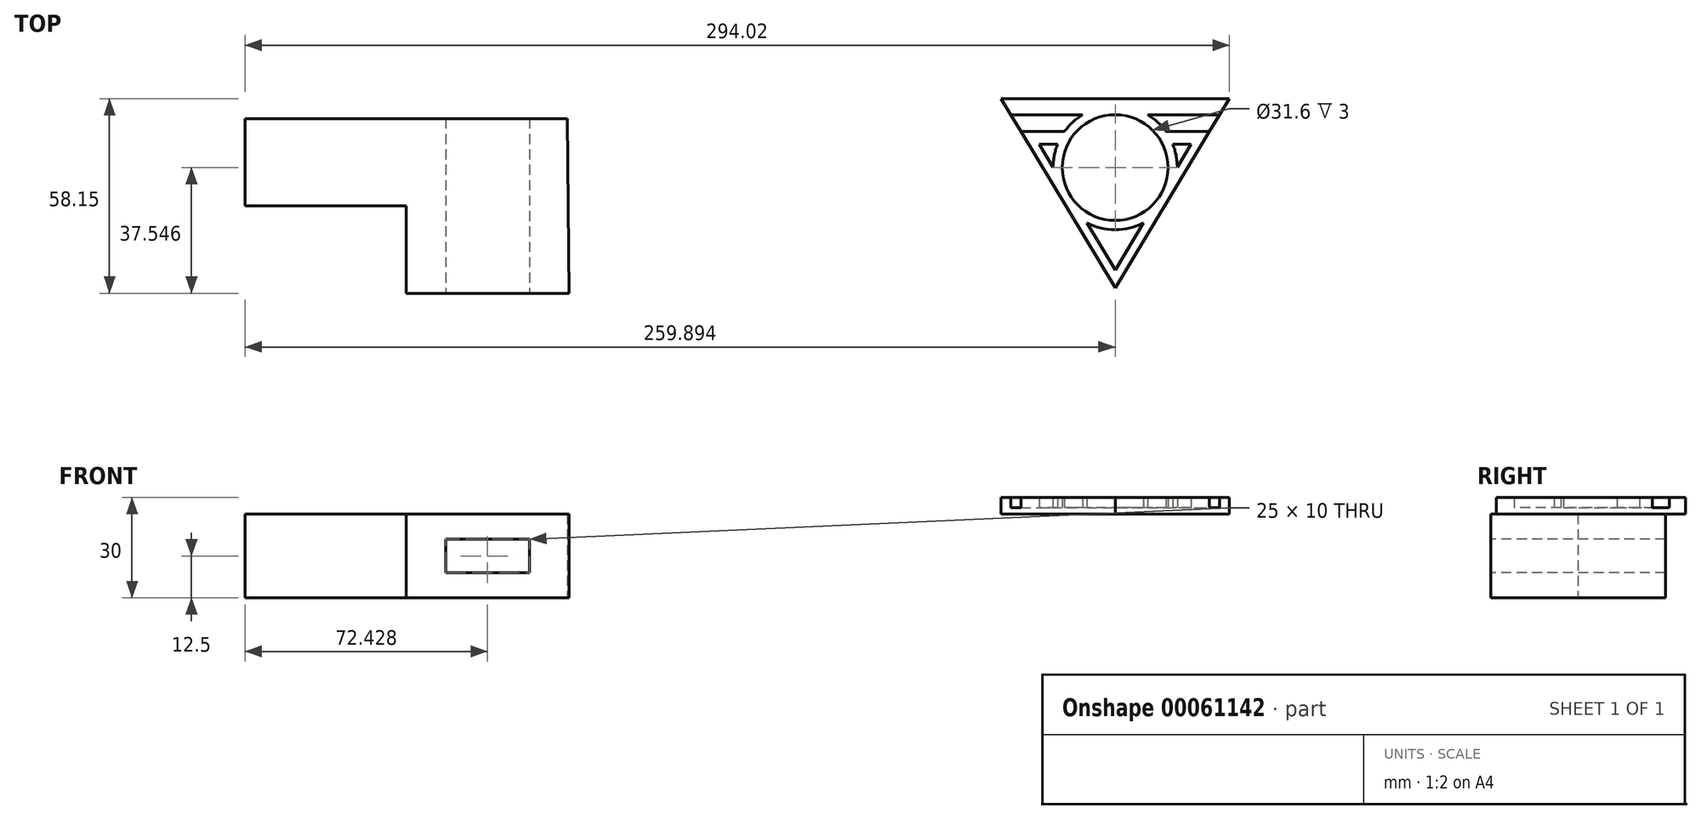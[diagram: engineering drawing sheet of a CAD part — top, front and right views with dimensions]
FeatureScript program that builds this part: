
annotation { "Feature Type Name" : "Feature", "Feature Type Description" : "" }
export const myFeature = defineFeature(function(context is Context, id is Id, definition is map)
    precondition{}
    {
        {
            var Q0;
            Q0=qCreatedBy(makeId("Top.planeOp"),FACE);
            var sketch = newSketch(context, id + "F0", { "sketchPlane" : qUnion([Q0])});
            skLineSegment(sketch, "E0", {"start": v(-34, 20.87) * mm, "end": v(62.24, 20.87) * mm});
            skLineSegment(sketch, "E1", {"start": v(62.24, 20.87) * mm, "end": v(62.74, -31.3) * mm});
            skLineSegment(sketch, "E2", {"start": v(62.74, -31.3) * mm, "end": v(14.12, -31.3) * mm});
            skPoint(sketch, "E2.endSnap0", {"position": v(14.12, 20.87) * mm});
            skLineSegment(sketch, "E3", {"start": v(14.12, -31.3) * mm, "end": v(14.12, -5.21) * mm});
            skPoint(sketch, "E3.endSnap0", {"position": v(62.49, -5.21) * mm});
            skLineSegment(sketch, "E4", {"start": v(14.12, -5.21) * mm, "end": v(-34, -5.21) * mm});
            skLineSegment(sketch, "E5", {"start": v(-34, -5.21) * mm, "end": v(-34, 20.87) * mm});
            skSolve(sketch);
        }
        {
            var Q0;
            Q0 = qSketchRegion(id + "F0", true);
            extrude(context, id + "F1", {"entities" : qUnion([Q0]), "depth" : 25 * mm});
        }
        {
            var Q0;
            Q0=makeQuery(id+"F1.opExtrude","SWEPT_FACE",FACE,{"disambiguationData":[OSD([sQuery(id+"F0.wireOp",EDGE,"E2")])]});
            var sketch = newSketch(context, id + "F2", { "sketchPlane" : qUnion([Q0])});
            skLineSegment(sketch, "E6.rect.bottom", {"start": v(50.93, 7.5) * mm, "end": v(25.93, 7.5) * mm});
            skLineSegment(sketch, "E6.rect.top", {"start": v(50.93, 17.5) * mm, "end": v(25.93, 17.5) * mm});
            skLineSegment(sketch, "E6.rect.left", {"start": v(50.93, 7.5) * mm, "end": v(50.93, 17.5) * mm});
            skLineSegment(sketch, "E6.rect.right", {"start": v(25.93, 7.5) * mm, "end": v(25.93, 17.5) * mm});
            skPoint(sketch, "E6.rect.middle", {"position": v(38.43, 12.5) * mm});
            skPoint(sketch, "E6.rect.middle.positionSnap0", {"position": v(62.74, 12.5) * mm});
            skPoint(sketch, "E6.rect.middle.positionSnap1", {"position": v(38.43, 25) * mm});
            skPoint(sketch, "E6.rect.centerSnap0", {"position": v(62.74, 12.5) * mm});
            skPoint(sketch, "E6.rect.centerSnap1", {"position": v(38.43, 25) * mm});
            skSolve(sketch);
        }
        {
            var Q0;
            Q0 = qSketchRegion(id + "F2", true);
            extrude(context, id + "F3", {"entities" : qUnion([Q0]), "operationType" : NewBodyOperationType.REMOVE, "endBound" : BoundingType.THROUGH_ALL, "oppositeDirection" : true, "depth" : 57.6 * mm});
        }
        {
            var Q0;
            Q0=makeQuery(id+"F1.opExtrude","CAP_FACE",FACE,{"disambiguationData":[OSD([sQuery(id+"F0.wireOp",EDGE,"E0"),sQuery(id+"F0.wireOp",EDGE,"E1"),sQuery(id+"F0.wireOp",EDGE,"E2"),sQuery(id+"F0.wireOp",EDGE,"E3"),sQuery(id+"F0.wireOp",EDGE,"E4"),sQuery(id+"F0.wireOp",EDGE,"E5")])],"isStart":false});
            var sketch = newSketch(context, id + "F4", { "sketchPlane" : qUnion([Q0])});
            skLineSegment(sketch, "E7", {"start": v(225.9, -29.64) * mm, "end": v(191.77, 26.85) * mm});
            skLineSegment(sketch, "E8", {"start": v(191.77, 26.85) * mm, "end": v(225.9, 26.85) * mm});
            skLineSegment(sketch, "E9", {"start": v(225.9, 26.85) * mm, "end": v(225.9, -29.64) * mm, "construction": true});
            skLineSegment(sketch, "E10.MirrorCS", {"start": v(260.02, 26.85) * mm, "end": v(225.9, 26.85) * mm});
            skLineSegment(sketch, "E11.MirrorCS", {"start": v(225.9, -29.64) * mm, "end": v(260.02, 26.85) * mm});
            skSolve(sketch);
        }
        {
            var Q0;
            Q0 = qSketchRegion(id + "F4", true);
            extrude(context, id + "F5", {"entities" : qUnion([Q0]), "depth" : 2 * mm});
        }
        {
            var Q0;
            Q0=makeQuery(id+"F5.opExtrude","CAP_FACE",FACE,{"disambiguationData":[OSD([sQuery(id+"F4.wireOp",EDGE,"E7"),sQuery(id+"F4.wireOp",EDGE,"E8"),sQuery(id+"F4.wireOp",EDGE,"E10.MirrorCS"),sQuery(id+"F4.wireOp",EDGE,"E11.MirrorCS")])],"isStart":false});
            var sketch = newSketch(context, id + "F6", { "sketchPlane" : qUnion([Q0])});
            skLineSegment(sketch, "E12", {"start": v(191.77, 26.85) * mm, "end": v(194.67, 22.05) * mm});
            skLineSegment(sketch, "E13", {"start": v(194.67, 22.05) * mm, "end": v(216.16, 22.05) * mm});
            skLineSegment(sketch, "E14", {"start": v(257.12, 22.05) * mm, "end": v(260.02, 26.85) * mm});
            skLineSegment(sketch, "E15", {"start": v(260.02, 26.85) * mm, "end": v(191.77, 26.85) * mm});
            skLineSegment(sketch, "E16", {"start": v(197.73, 16.97) * mm, "end": v(210.75, 16.97) * mm});
            skLineSegment(sketch, "E17", {"start": v(254.06, 16.97) * mm, "end": v(251.77, 13.2) * mm});
            skLineSegment(sketch, "E18", {"start": v(251.77, 13.2) * mm, "end": v(243.1, 13.2) * mm});
            skLineSegment(sketch, "E19", {"start": v(200.02, 13.2) * mm, "end": v(197.73, 16.97) * mm});
            skLineSegment(sketch, "E20", {"start": v(225.9, -29.64) * mm, "end": v(225.9, 26.85) * mm, "construction": true});
            skLineSegment(sketch, "E21", {"start": v(203.23, 13.2) * mm, "end": v(207.34, 6.4) * mm});
            skLineSegment(sketch, "E22.MirrorCS", {"start": v(248.55, 13.2) * mm, "end": v(244.45, 6.4) * mm});
            skArc(sketch, "E23", {"start": v(216.16, 22.05) * mm, "mid": v(213.2, 19.78) * mm, "end": v(210.75, 16.97) * mm});
            skCircle(sketch, "E24", {"center": v(225.9, 6.25) * mm, "radius": 15.8 * mm});
            skLineSegment(sketch, "E25.trimOffspring", {"start": v(235.63, 22.05) * mm, "end": v(257.12, 22.05) * mm});
            skLineSegment(sketch, "E26.trimOffspring", {"start": v(208.69, 13.2) * mm, "end": v(203.23, 13.2) * mm});
            skArc(sketch, "E27.trimOffspring", {"start": v(208.69, 13.2) * mm, "mid": v(207.7, 9.86) * mm, "end": v(207.34, 6.4) * mm});
            skArc(sketch, "E28.trimOffspring", {"start": v(217.4, -10.25) * mm, "mid": v(238.4, -7.47) * mm, "end": v(243.1, 13.2) * mm});
            skLineSegment(sketch, "E29.trimOffspring", {"start": v(217.4, -10.25) * mm, "end": v(225.9, -24.31) * mm});
            skLineSegment(sketch, "E30.trimOffspring", {"start": v(234.39, -10.25) * mm, "end": v(225.9, -24.31) * mm});
            skLineSegment(sketch, "E31.trimOffspring", {"start": v(241.04, 16.97) * mm, "end": v(254.06, 16.97) * mm});
            skArc(sketch, "E32.trimOffspring", {"start": v(241.04, 16.97) * mm, "mid": v(238.59, 19.78) * mm, "end": v(235.63, 22.05) * mm});
            skSolve(sketch);
        }
        {
            var Q0;
            Q0=makeQuery(id+"F6.imprint","IMPRINT",FACE,{"disambiguationData":[TD([[makeQuery(id+"F6.imprint","IMPRINT",EDGE,{"derivedFrom":sQuery(id+"F6.wireOp",EDGE,"E12")}),-1.0]])]});
            var Q1;
            {var subQ3=sQuery(id+"F6.wireOp",EDGE,"E22.MirrorCS");Q1=makeQuery(id+"F6.imprint","IMPRINT",FACE,{"disambiguationData":[TD([[makeQuery(id+"F6.imprint","IMPRINT",EDGE,{"derivedFrom":subQ3}),1.0]])]});}
            extrude(context, id + "F7", {"entities" : qUnion([Q0, Q1]), "operationType" : NewBodyOperationType.ADD, "depth" : 3 * mm});
        }
    });
